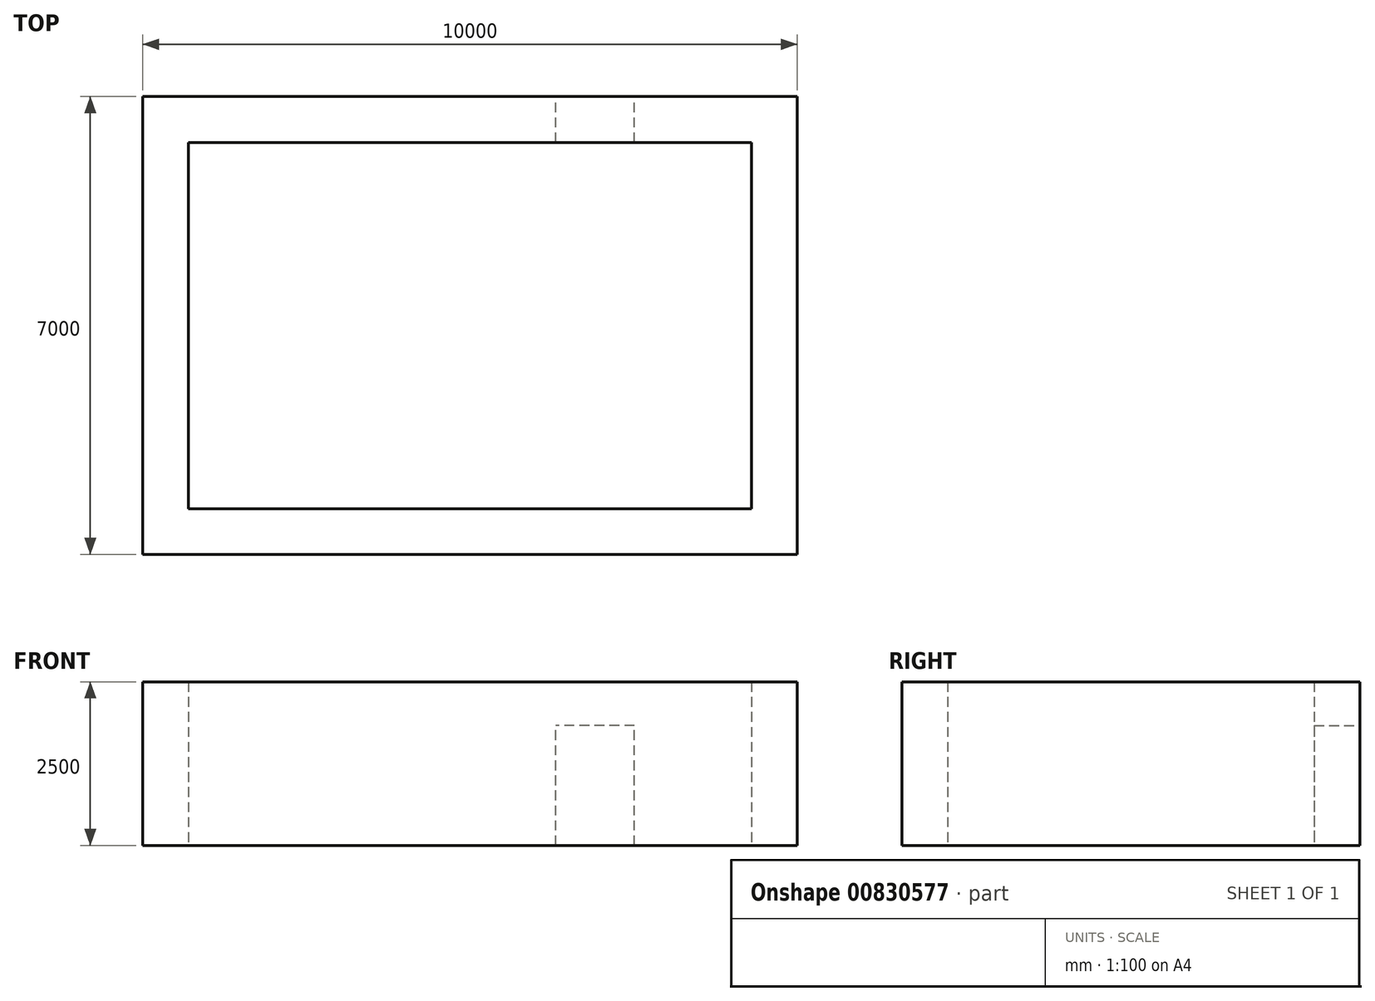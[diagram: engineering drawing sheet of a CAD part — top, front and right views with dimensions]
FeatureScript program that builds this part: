
annotation { "Feature Type Name" : "Feature", "Feature Type Description" : "" }
export const myFeature = defineFeature(function(context is Context, id is Id, definition is map)
    precondition{}
    {
        {
            var Q0;
            Q0=qCreatedBy(makeId("Top.planeOp"),FACE);
            var sketch = newSketch(context, id + "F0", { "sketchPlane" : qUnion([Q0])});
            skLineSegment(sketch, "E0.bottom", {"start": v(0, 0) * mm, "end": v(10000, 0) * mm});
            skLineSegment(sketch, "E0.top", {"start": v(0, 7000) * mm, "end": v(10000, 7000) * mm});
            skLineSegment(sketch, "E0.left", {"start": v(0, 0) * mm, "end": v(0, 7000) * mm});
            skLineSegment(sketch, "E0.right", {"start": v(10000, 0) * mm, "end": v(10000, 7000) * mm});
            skLineSegment(sketch, "E1.0", {"start": v(700, 6300) * mm, "end": v(9300, 6300) * mm});
            skLineSegment(sketch, "E1.1", {"start": v(700, 700) * mm, "end": v(700, 6300) * mm});
            skLineSegment(sketch, "E1.2", {"start": v(700, 700) * mm, "end": v(9300, 700) * mm});
            skLineSegment(sketch, "E1.3", {"start": v(9300, 700) * mm, "end": v(9300, 6300) * mm});
            skLineSegment(sketch, "E2.bottom", {"start": v(6313.2, 7000) * mm, "end": v(7513.2, 7000) * mm});
            skLineSegment(sketch, "E2.top", {"start": v(6313.2, 6300) * mm, "end": v(7513.2, 6300) * mm});
            skLineSegment(sketch, "E2.left", {"start": v(6313.2, 7000) * mm, "end": v(6313.2, 6300) * mm});
            skLineSegment(sketch, "E2.right", {"start": v(7513.2, 7000) * mm, "end": v(7513.2, 6300) * mm});
            skSolve(sketch);
        }
        {
            var Q0;
            Q0=makeQuery(id+"F0.imprint","IMPRINT",FACE,{"disambiguationData":[TD([[makeQuery(id+"F0.imprint","IMPRINT",EDGE,{"derivedFrom":sQuery(id+"F0.wireOp",EDGE,"E0.bottom")}),1.0]])]});
            var Q1;
            {var subQ2=sQuery(id+"F0.wireOp",EDGE,"E2.left");Q1=makeQuery(id+"F0.imprint","IMPRINT",FACE,{"disambiguationData":[TD([[makeQuery(id+"F0.imprint","IMPRINT",EDGE,{"derivedFrom":subQ2}),1.0]])]});}
            extrude(context, id + "F1", {"entities" : qUnion([Q0, Q1]), "depth" : 2500 * mm, "offsetDistance" : 25 * mm});
        }
        {
            var Q0;
            Q0=makeQuery(id+"F1.opExtrude","SWEPT_FACE",FACE,{"disambiguationData":[OSD([sQuery(id+"F0.wireOp",EDGE,"E0.top")])]});
            var sketch = newSketch(context, id + "F2", { "sketchPlane" : qUnion([Q0])});
            skLineSegment(sketch, "E3.bottom", {"start": v(-7513.2, 0) * mm, "end": v(-6313.2, 0) * mm});
            skLineSegment(sketch, "E3.top", {"start": v(-7513.2, 1833.16) * mm, "end": v(-6313.2, 1833.16) * mm});
            skLineSegment(sketch, "E3.left", {"start": v(-7513.2, 0) * mm, "end": v(-7513.2, 1833.16) * mm});
            skLineSegment(sketch, "E3.right", {"start": v(-6313.2, 0) * mm, "end": v(-6313.2, 1833.16) * mm});
            skSolve(sketch);
        }
        {
            var Q0;
            Q0=makeQuery(id+"F2.imprint","IMPRINT",FACE,{"disambiguationData":[TD([[makeQuery(id+"F2.imprint","IMPRINT",EDGE,{"derivedFrom":sQuery(id+"F2.wireOp",EDGE,"E3.bottom")}),-1.0]])]});
            extrude(context, id + "F3", {"entities" : qUnion([Q0]), "operationType" : NewBodyOperationType.REMOVE, "endBound" : BoundingType.UP_TO_NEXT, "oppositeDirection" : true, "depth" : 25 * mm, "offsetDistance" : 25 * mm});
        }
    });
